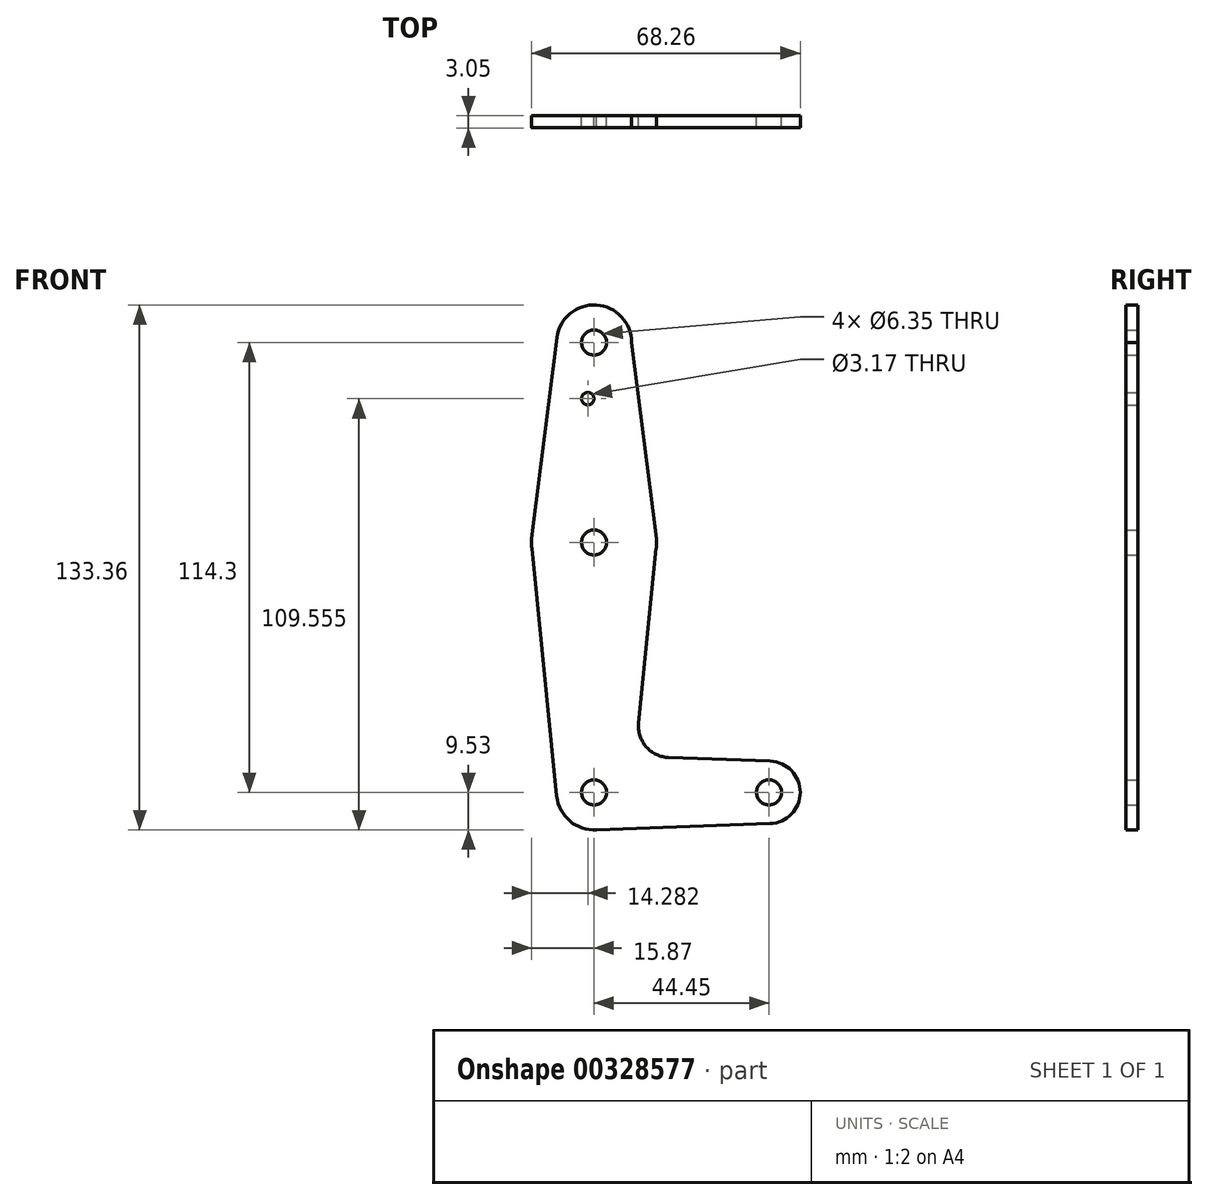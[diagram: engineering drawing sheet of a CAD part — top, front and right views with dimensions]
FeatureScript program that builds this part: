
annotation { "Feature Type Name" : "Feature", "Feature Type Description" : "" }
export const myFeature = defineFeature(function(context is Context, id is Id, definition is map)
    precondition{}
    {
        {
            var Q0;
            Q0=qCreatedBy(makeId("Front.planeOp"),FACE);
            var sketch = newSketch(context, id + "F0", { "sketchPlane" : qUnion([Q0])});
            skLineSegment(sketch, "E0", {"start": v(0, 0) * mm, "end": v(0, 114.3) * mm, "construction": true});
            skLineSegment(sketch, "E1", {"start": v(0, 0) * mm, "end": v(44.45, 0) * mm, "construction": true});
            skCircle(sketch, "E2", {"center": v(0, 0) * mm, "radius": 9.53 * mm});
            skCircle(sketch, "E3", {"center": v(44.45, 0) * mm, "radius": 7.94 * mm});
            skCircle(sketch, "E4", {"center": v(0, 63.5) * mm, "radius": 15.88 * mm});
            skCircle(sketch, "E5", {"center": v(0, 114.3) * mm, "radius": 9.53 * mm});
            skLineSegment(sketch, "E6", {"start": v(0, -9.53) * mm, "end": v(44.73, -7.93) * mm});
            skLineSegment(sketch, "E7", {"start": v(-9.45, 115.5) * mm, "end": v(-15.75, 65.48) * mm});
            skLineSegment(sketch, "E8", {"start": v(9.53, 114.3) * mm, "end": v(15.75, 65.5) * mm});
            skCircle(sketch, "E9", {"center": v(0, 63.5) * mm, "radius": 3.18 * mm});
            skCircle(sketch, "E10", {"center": v(0, 0) * mm, "radius": 3.18 * mm});
            skCircle(sketch, "E11", {"center": v(44.45, 0) * mm, "radius": 3.18 * mm});
            skCircle(sketch, "E12", {"center": v(0, 114.3) * mm, "radius": 3.18 * mm});
            skPoint(sketch, "E13.centerSnap0", {"position": v(12.64, 89.9) * mm});
            skCircle(sketch, "E14", {"center": v(-1.59, 100.03) * mm, "radius": 1.59 * mm});
            skLineSegment(sketch, "E15", {"start": v(-9.48, -0.95) * mm, "end": v(-15.8, 61.91) * mm});
            skLineSegment(sketch, "E16", {"start": v(11.34, 17.59) * mm, "end": v(15.8, 61.91) * mm});
            skLineSegment(sketch, "E17", {"start": v(18.97, 8.85) * mm, "end": v(44.73, 7.93) * mm});
            skArc(sketch, "E18.filletArc", {"start": v(11.34, 17.59) * mm, "mid": v(13.26, 11.57) * mm, "end": v(18.97, 8.85) * mm});
            skSolve(sketch);
        }
        {
            var Q0;
            Q0 = qSketchRegion(id + "F0", true);
            extrude(context, id + "F1", {"entities" : qUnion([Q0]), "depth" : 3.05 * mm});
        }
    });
